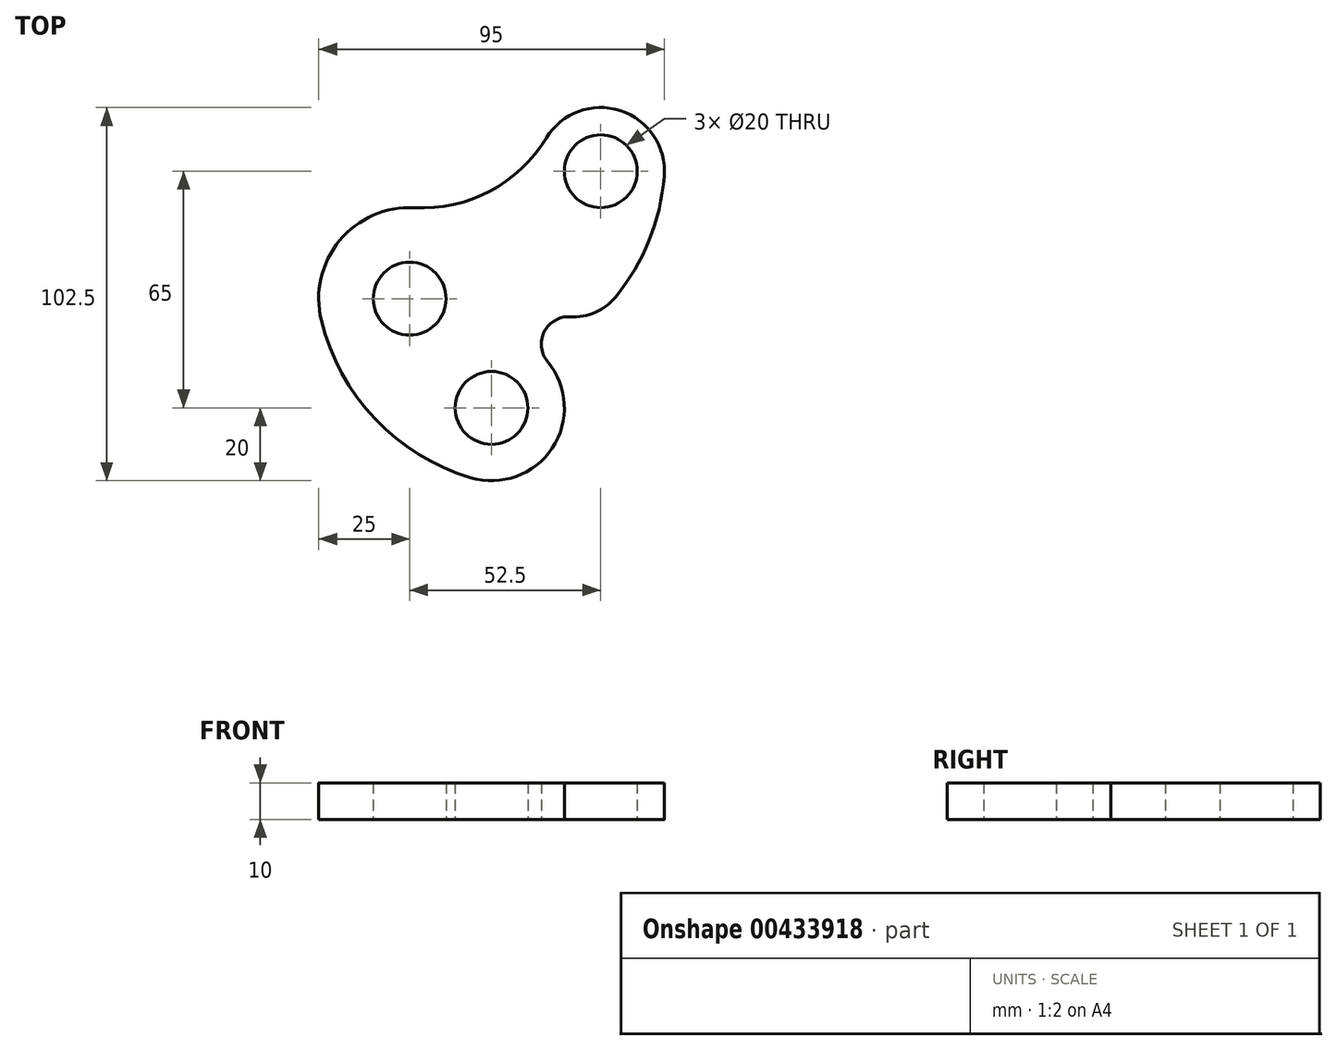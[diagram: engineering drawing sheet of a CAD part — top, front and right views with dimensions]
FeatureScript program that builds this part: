
annotation { "Feature Type Name" : "Feature", "Feature Type Description" : "" }
export const myFeature = defineFeature(function(context is Context, id is Id, definition is map)
    precondition{}
    {
        {
            var Q0;
            Q0=qCreatedBy(makeId("Top.planeOp"),FACE);
            var sketch = newSketch(context, id + "F0", { "sketchPlane" : qUnion([Q0])});
            skCircle(sketch, "E0", {"center": v(0, 0) * mm, "radius": 10 * mm});
            skCircle(sketch, "E1", {"center": v(52.5, 35) * mm, "radius": 10 * mm});
            skCircle(sketch, "E2", {"center": v(22.5, -30) * mm, "radius": 10 * mm});
            skArc(sketch, "E3", {"start": v(-24.28, -5.94) * mm, "mid": v(-19.26, 15.94) * mm, "end": v(1.3, 24.97) * mm});
            skArc(sketch, "E4", {"start": v(37.55, 44.1) * mm, "mid": v(57.9, 51.64) * mm, "end": v(69.94, 33.58) * mm});
            skArc(sketch, "E5", {"start": v(37.9, -17.24) * mm, "mid": v(39.17, -41.05) * mm, "end": v(16.75, -49.16) * mm});
            skArc(sketch, "E6", {"start": v(-24.28, -5.94) * mm, "mid": v(-9.51, -33) * mm, "end": v(16.75, -49.16) * mm});
            skArc(sketch, "E7", {"start": v(1.3, 24.97) * mm, "mid": v(22.07, 29.54) * mm, "end": v(37.55, 44.1) * mm});
            skArc(sketch, "E8", {"start": v(56.62, 0.51) * mm, "mid": v(51.03, -3.73) * mm, "end": v(44.12, -4.97) * mm});
            skArc(sketch, "E9", {"start": v(44.12, -4.97) * mm, "mid": v(37, -9.07) * mm, "end": v(37.9, -17.24) * mm});
            skArc(sketch, "E10", {"start": v(56.62, 0.51) * mm, "mid": v(65.8, 16.03) * mm, "end": v(69.94, 33.58) * mm});
            skSolve(sketch);
        }
        {
            var Q0;
            Q0=makeQuery(id+"F0.imprint","IMPRINT",FACE,{"disambiguationData":[TD([[makeQuery(id+"F0.imprint","IMPRINT",EDGE,{"derivedFrom":sQuery(id+"F0.wireOp",EDGE,"E0")}),-1.0]])]});
            extrude(context, id + "F1", {"entities" : qUnion([Q0]), "depth" : 10 * mm});
        }
    });
